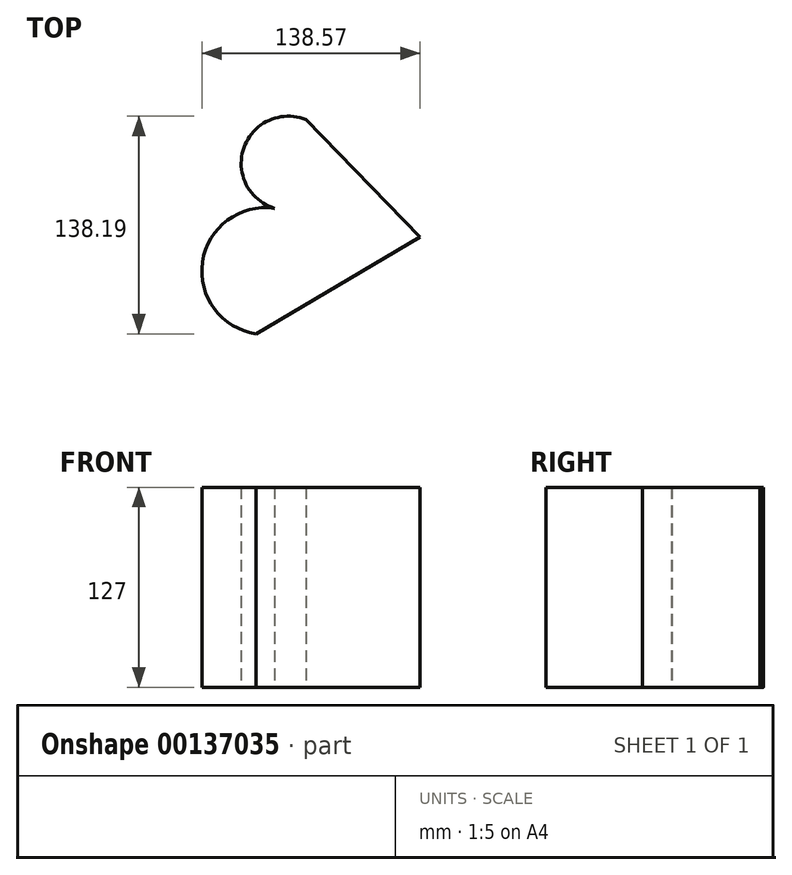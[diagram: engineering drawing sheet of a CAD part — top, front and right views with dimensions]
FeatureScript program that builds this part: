
annotation { "Feature Type Name" : "Feature", "Feature Type Description" : "" }
export const myFeature = defineFeature(function(context is Context, id is Id, definition is map)
    precondition{}
    {
        {
            var Q0;
            Q0=qCreatedBy(makeId("Top.planeOp"),FACE);
            var sketch = newSketch(context, id + "F0", { "sketchPlane" : qUnion([Q0])});
            skArc(sketch, "E0", {"start": v(-43.7, 33.2) * mm, "mid": v(-89.37, -0.83) * mm, "end": v(-55.34, -46.52) * mm});
            skArc(sketch, "E1", {"start": v(-23.72, 89.49) * mm, "mid": v(-63.1, 71.77) * mm, "end": v(-43.7, 33.2) * mm});
            skLineSegment(sketch, "E2", {"start": v(-55.34, -46.52) * mm, "end": v(48.77, 14.85) * mm});
            skPoint(sketch, "E3.end.orphan", {"position": v(8.85, 14.85) * mm});
            skLineSegment(sketch, "E4", {"start": v(-23.72, 89.49) * mm, "end": v(48.77, 14.85) * mm});
            skSolve(sketch);
        }
        {
            var Q0;
            Q0=makeQuery(id+"F0.imprint","IMPRINT",FACE,{"disambiguationData":[TD([[makeQuery(id+"F0.imprint","IMPRINT",EDGE,{"derivedFrom":sQuery(id+"F0.wireOp",EDGE,"E0")}),1.0]])]});
            extrude(context, id + "F1", {"entities" : qUnion([Q0]), "depth" : 127 * mm});
        }
    });
